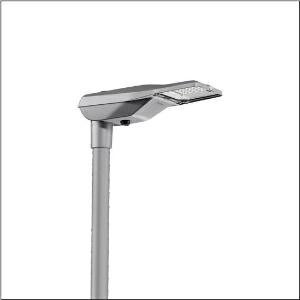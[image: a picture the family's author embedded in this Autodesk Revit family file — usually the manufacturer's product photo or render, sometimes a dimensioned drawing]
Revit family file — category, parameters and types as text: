
# Revit family: streetlight_sl_21_iq_micro___p0_8ab_5xe1r31u08db_7cfa
name_source: partatom
category: Lighting Fixtures
units: mm (PartAtom-declared; Revit-internal decimal feet)

## family parameters
Cut with Voids When Loaded = No
Host = Face
Light Source = No
Part Type = Normal
Room Calculation Point = No
Round Connector Dimension = Use Diameter
Shared = No

## types (1)
- --- (1 x LED, 4550 lm, 39.1 W, 3000K)
    Apparent Load = 39 VA
    CIE Flux Codes = 36 71 98 100 100
    Color Rendering = 70
    Color Temperature = 3000K
    Default Elevation = 1800 mm
    Description = Streetlight SL 21 iQ micro, mast luminaire, primary light control with lens, of PMMA, primary optical cover: cover, of toughened safety glass, transparent, light distribution: P0.8aB, light emission: direct distribution, primary light characteristic: asymmetric, installation type: post-top, side-entry, LED, High Power LED, rated luminous flux: 4.550lm, luminous efficacy: 116lm/W, light colour: 730, colour temperature: 3000K, control gear: iQ-Street Remote, D4i with power reduction, control: pre-setting: logarithmic dimming characteristic, Street-Remote, Auto-Match, Temp-Guard, Lumen-Switch, Night-Set, Smart-Wire, Light-Fading, Desk-Remote (wireless, voltage-free reading and setting of iQ features in the workshop via application-optimized NFC function/RFID function), optimised constant luminous flux control (CLO 2.0), mains connection: 220..240V, AC, 50/60Hz, start of lifetime: 39W, end of service life: 41W, reduction: 17W, luminaire housing, of diecast aluminium, powder-coated, Siteco® metallic grey (DB 702S), corrosivity category C5 high according to DIN EN ISO 12944, please order mast flange separately, inclination adjustable: 0°, 5°, 10°, 15°, sealing non-destructively replaceable, multi-level sealing system, length: 528mm, width: 235mm, height: 110mm, mast flange for spigot size: 42mm (side-entry): 5XC10008XM4, 60/48mm (side-entry/post-top): 5XC10108XM2, 76/60mm (side-entry/post-top): 5XC10108XM1, mounting height: 4..8m, Smart Interface below, protection rating (complete): IP66, insulation class (complete): insulation class II (safety insulation), certification: CE, ENEC, ENEC+, VDE, impact resistance: IK10, permissible operating ambient temperature for outdoor applications: -40..+50°C, standard-compliant lighting for roads and squares, packaging unit: 1 piece

Light Distribution: P0.8aB
    Height = 110 mm
    Lamp = 1 x LED
    Lamp Light Flux = 4550 lm
    Lamp Power = 39.1 W
    Lamp count = 1
    Length = 528 mm
    Luminous efficacy = 116 lm/W
    Manufacturer = Siteco
    ModVariant = No
    Model = 5XE1R31U08DB
    Number of Poles = 1
    OnlyDefault = Yes
    Power Factor = 1
    Product Name = Streetlight SL 21 iQ micro | P0.8aB
    Product group = mast luminaire | pylon top
    ProductGroupID = 6100
    Protection Class = Protection class II
    Protection Degree = IP 66
    RLX_Detail_Level = 1
    RLX_Emergency_Light_Flux = 0 lm
    RLX_Emergency_Type = 0
    RLX_Emergency_Type_DB = No
    RlxData = <blob elided: 99349 chars, md5=7f64a1e4>
    Socket = socket
    Standby Power = 0 W
    System Light Flux = 4550 lm
    System Power = 39 W
    Type Comments = factory setting: luminous flux: 100 % | dim-lin: 254 | 765 mA
    Type Image = l_1277290.jpg
    URL = http://relux.com
    VarID = @adj_086115
    Voltage = 0 V
    Weight = 0.00 kg
    Width = 235 mm

## geometry (parser evidence)
native form markers: Blend x4, Sweep x10
no freeform markers — native parametric forms only
